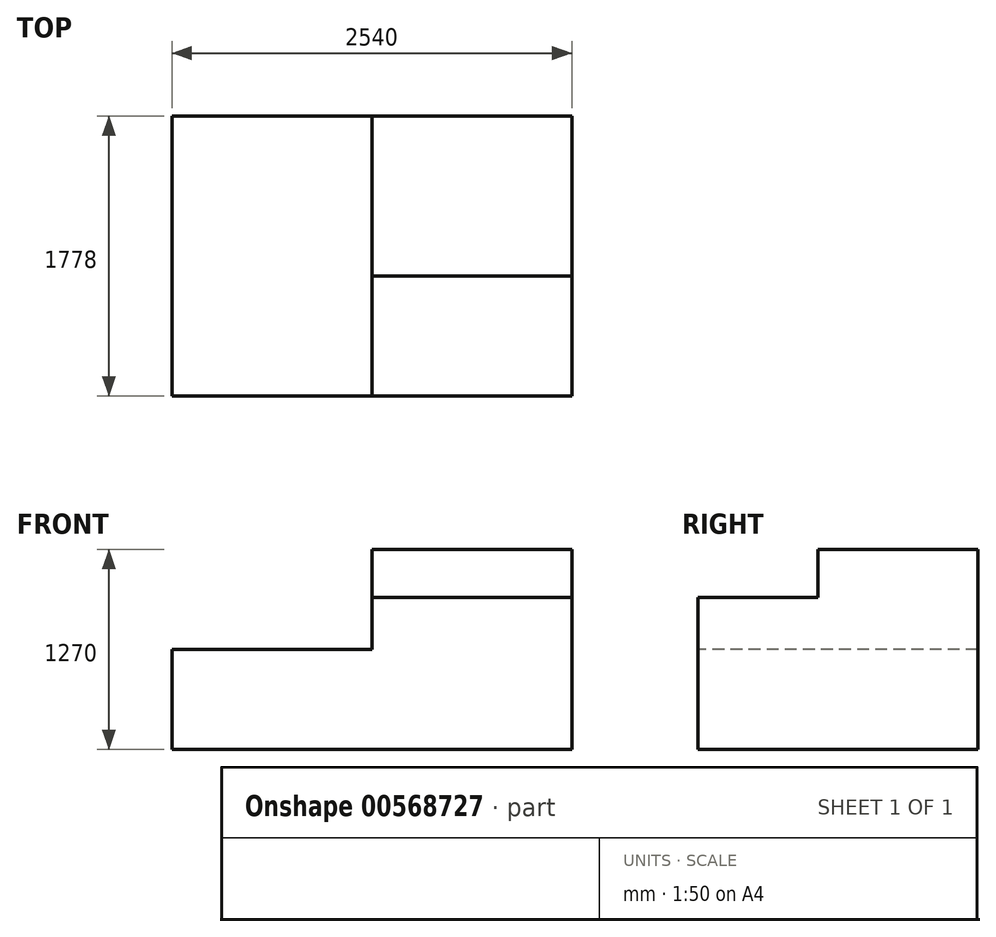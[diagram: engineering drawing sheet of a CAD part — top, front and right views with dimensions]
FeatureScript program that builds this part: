
annotation { "Feature Type Name" : "Feature", "Feature Type Description" : "" }
export const myFeature = defineFeature(function(context is Context, id is Id, definition is map)
    precondition{}
    {
        {
            var Q0;
            Q0=qCreatedBy(makeId("Top.planeOp"),FACE);
            var sketch = newSketch(context, id + "F0", { "sketchPlane" : qUnion([Q0])});
            skLineSegment(sketch, "E0.bottom", {"start": v(0, 0) * mm, "end": v(2540, 0) * mm});
            skLineSegment(sketch, "E0.top", {"start": v(0, 1778) * mm, "end": v(2540, 1778) * mm});
            skLineSegment(sketch, "E0.left", {"start": v(0, 0) * mm, "end": v(0, 1778) * mm});
            skLineSegment(sketch, "E0.right", {"start": v(2540, 0) * mm, "end": v(2540, 1778) * mm});
            skSolve(sketch);
        }
        {
            var Q0;
            Q0=makeQuery(id+"F0.imprint","IMPRINT",FACE,{"disambiguationData":[TD([[makeQuery(id+"F0.imprint","IMPRINT",EDGE,{"derivedFrom":sQuery(id+"F0.wireOp",EDGE,"E0.bottom")}),1.0]])]});
            extrude(context, id + "F1", {"entities" : qUnion([Q0]), "depth" : 1270 * mm, "offsetDistance" : 25.4 * mm});
        }
        {
            var Q0;
            Q0=makeQuery(id+"F1.opExtrude","SWEPT_FACE",FACE,{"disambiguationData":[OSD([sQuery(id+"F0.wireOp",EDGE,"E0.bottom")])]});
            var sketch = newSketch(context, id + "F2", { "sketchPlane" : qUnion([Q0])});
            skLineSegment(sketch, "E1.bottom", {"start": v(0, 1270) * mm, "end": v(1270, 1270) * mm});
            skLineSegment(sketch, "E1.top", {"start": v(0, 635) * mm, "end": v(1270, 635) * mm});
            skLineSegment(sketch, "E1.left", {"start": v(0, 1270) * mm, "end": v(0, 635) * mm});
            skLineSegment(sketch, "E1.right", {"start": v(1270, 1270) * mm, "end": v(1270, 635) * mm});
            skSolve(sketch);
        }
        {
            var Q0;
            Q0=makeQuery(id+"F2.imprint","IMPRINT",FACE,{"disambiguationData":[TD([[makeQuery(id+"F2.imprint","IMPRINT",EDGE,{"derivedFrom":sQuery(id+"F2.wireOp",EDGE,"E1.bottom")}),-1.0]])]});
            extrude(context, id + "F3", {"entities" : qUnion([Q0]), "operationType" : NewBodyOperationType.REMOVE, "endBound" : BoundingType.THROUGH_ALL, "oppositeDirection" : true, "depth" : 25.4 * mm, "offsetDistance" : 25.4 * mm});
        }
        {
            var Q0;
            Q0=makeQuery(id+"F1.opExtrude","SWEPT_FACE",FACE,{"disambiguationData":[OSD([sQuery(id+"F0.wireOp",EDGE,"E0.bottom")])]});
            var sketch = newSketch(context, id + "F4", { "sketchPlane" : qUnion([Q0])});
            skLineSegment(sketch, "E2.bottom", {"start": v(1270, 1270) * mm, "end": v(2540, 1270) * mm});
            skLineSegment(sketch, "E2.top", {"start": v(1270, 965.2) * mm, "end": v(2540, 965.2) * mm});
            skLineSegment(sketch, "E2.left", {"start": v(1270, 1270) * mm, "end": v(1270, 965.2) * mm});
            skLineSegment(sketch, "E2.right", {"start": v(2540, 1270) * mm, "end": v(2540, 965.2) * mm});
            skSolve(sketch);
        }
        {
            var Q0;
            Q0=makeQuery(id+"F4.imprint","IMPRINT",FACE,{"disambiguationData":[TD([[makeQuery(id+"F4.imprint","IMPRINT",EDGE,{"derivedFrom":sQuery(id+"F4.wireOp",EDGE,"E2.bottom")}),-1.0]])]});
            extrude(context, id + "F5", {"entities" : qUnion([Q0]), "operationType" : NewBodyOperationType.REMOVE, "oppositeDirection" : true, "depth" : 762 * mm, "offsetDistance" : 25.4 * mm});
        }
    });
